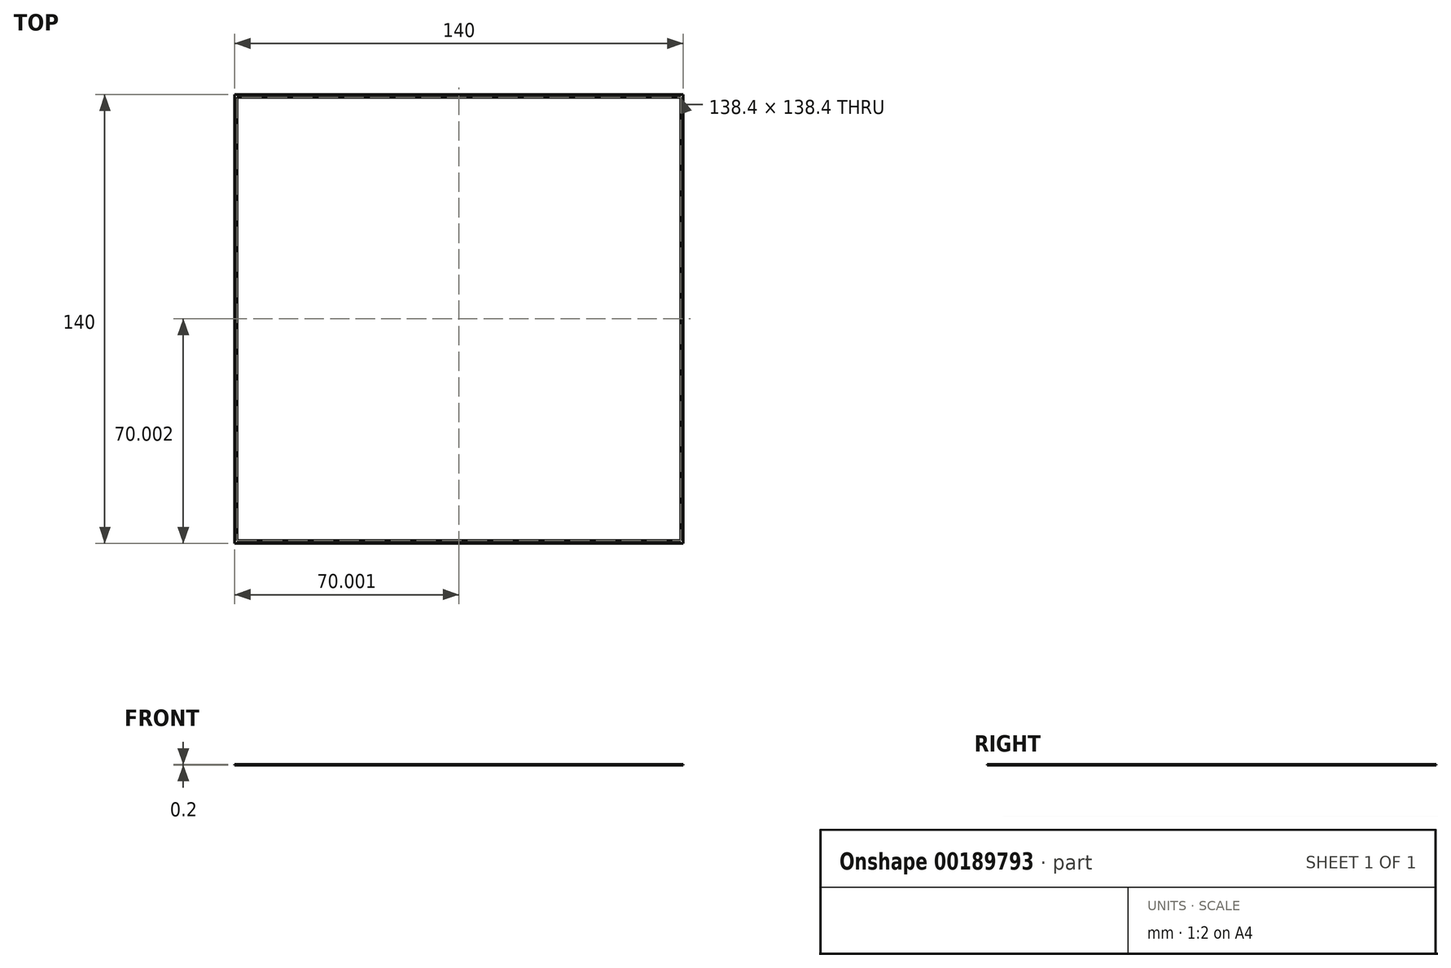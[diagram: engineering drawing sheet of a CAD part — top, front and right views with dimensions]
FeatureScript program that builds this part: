
annotation { "Feature Type Name" : "Feature", "Feature Type Description" : "" }
export const myFeature = defineFeature(function(context is Context, id is Id, definition is map)
    precondition{}
    {
        {
            var Q0;
            Q0=qCreatedBy(makeId("Top.planeOp"),FACE);
            var sketch = newSketch(context, id + "F0", { "sketchPlane" : qUnion([Q0])});
            skLineSegment(sketch, "E0.bottom", {"start": v(-71.3, 71.15) * mm, "end": v(68.7, 71.15) * mm});
            skLineSegment(sketch, "E0.top", {"start": v(-71.3, -68.85) * mm, "end": v(68.7, -68.85) * mm});
            skLineSegment(sketch, "E0.left", {"start": v(-71.3, 71.15) * mm, "end": v(-71.3, -68.85) * mm});
            skLineSegment(sketch, "E0.right", {"start": v(68.7, 71.15) * mm, "end": v(68.7, -68.85) * mm});
            skLineSegment(sketch, "E1.0", {"start": v(67.9, 70.35) * mm, "end": v(67.9, -68.05) * mm});
            skLineSegment(sketch, "E1.1", {"start": v(-70.5, 70.35) * mm, "end": v(67.9, 70.35) * mm});
            skLineSegment(sketch, "E1.2", {"start": v(-70.5, 70.35) * mm, "end": v(-70.5, -68.05) * mm});
            skLineSegment(sketch, "E1.3", {"start": v(-70.5, -68.05) * mm, "end": v(67.9, -68.05) * mm});
            skSolve(sketch);
        }
        {
            var Q0;
            Q0=makeQuery(id+"F0.imprint","IMPRINT",FACE,{"disambiguationData":[TD([[makeQuery(id+"F0.imprint","IMPRINT",EDGE,{"derivedFrom":sQuery(id+"F0.wireOp",EDGE,"E0.bottom")}),-1.0]])]});
            extrude(context, id + "F1", {"entities" : qUnion([Q0]), "depth" : 0.2 * mm});
        }
    });
